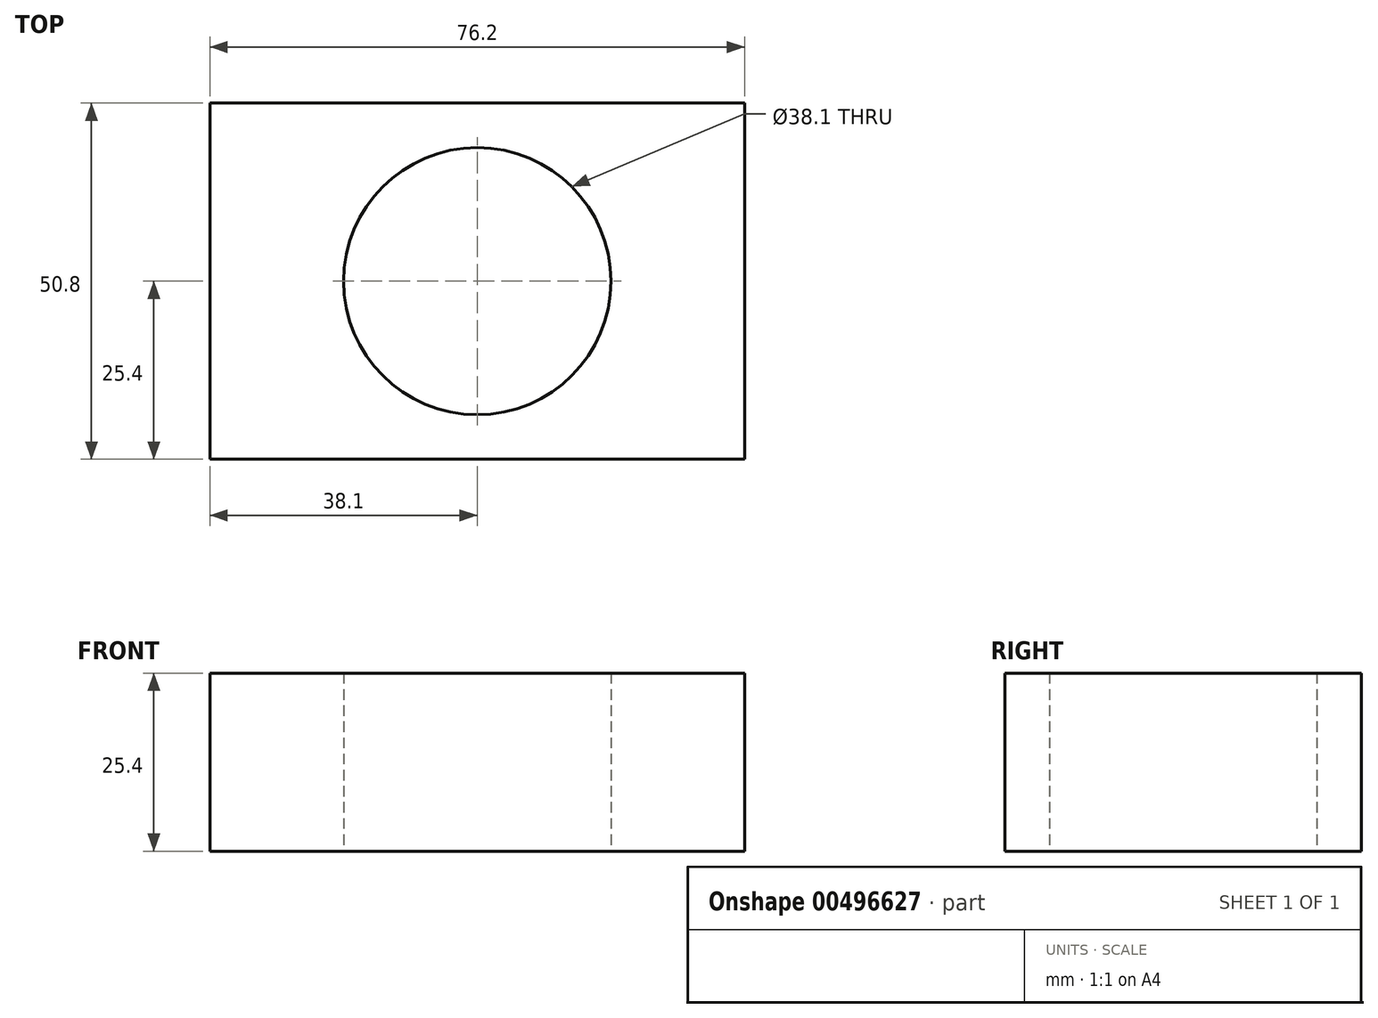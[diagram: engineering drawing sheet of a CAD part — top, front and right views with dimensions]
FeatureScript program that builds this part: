
annotation { "Feature Type Name" : "Feature", "Feature Type Description" : "" }
export const myFeature = defineFeature(function(context is Context, id is Id, definition is map)
    precondition{}
    {
        {
            var Q0;
            Q0=qCreatedBy(makeId("Top.planeOp"),FACE);
            var sketch = newSketch(context, id + "F0", { "sketchPlane" : qUnion([Q0])});
            skLineSegment(sketch, "E0.bottom", {"start": v(-38.1, 25.4) * mm, "end": v(38.1, 25.4) * mm});
            skLineSegment(sketch, "E0.top", {"start": v(-38.1, -25.4) * mm, "end": v(38.1, -25.4) * mm});
            skLineSegment(sketch, "E0.left", {"start": v(-38.1, 25.4) * mm, "end": v(-38.1, -25.4) * mm});
            skLineSegment(sketch, "E0.right", {"start": v(38.1, 25.4) * mm, "end": v(38.1, -25.4) * mm});
            skPoint(sketch, "E0.middle", {"position": v(0, 0) * mm});
            skCircle(sketch, "E1", {"center": v(0, 0) * mm, "radius": 19.05 * mm});
            skSolve(sketch);
        }
        {
            var Q0;
            Q0=makeQuery(id+"F0.imprint","IMPRINT",FACE,{"disambiguationData":[TD([[makeQuery(id+"F0.imprint","IMPRINT",EDGE,{"derivedFrom":sQuery(id+"F0.wireOp",EDGE,"E0.bottom")}),-1.0]])]});
            extrude(context, id + "F1", {"entities" : qUnion([Q0]), "depth" : 25.4 * mm, "offsetDistance" : 25.4 * mm});
        }
    });
